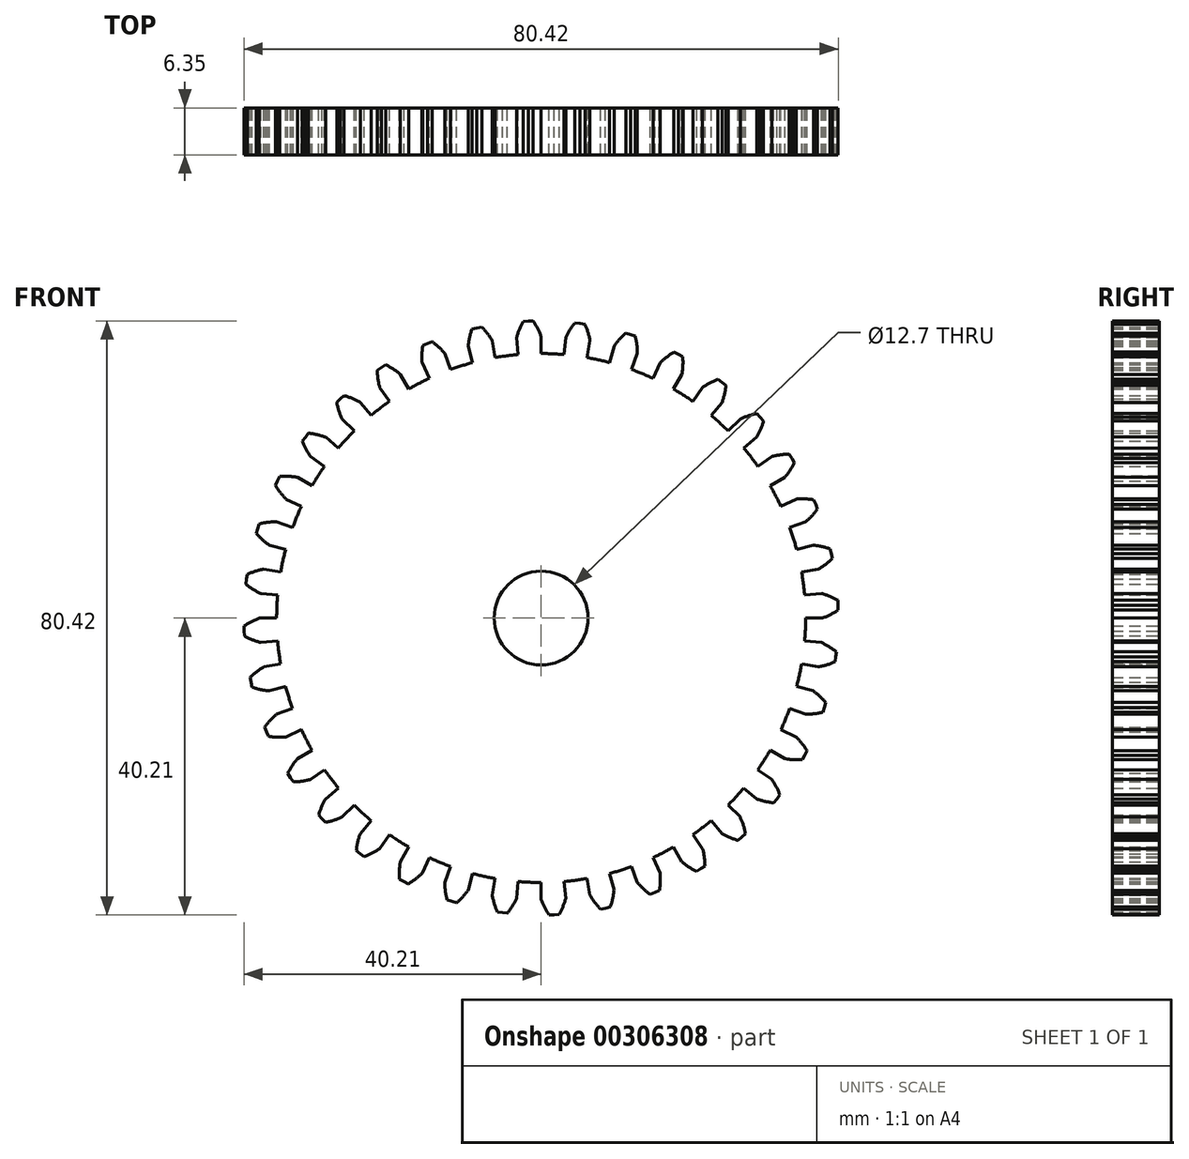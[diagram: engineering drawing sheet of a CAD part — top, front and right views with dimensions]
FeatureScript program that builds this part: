
annotation { "Feature Type Name" : "Feature", "Feature Type Description" : "" }
export const myFeature = defineFeature(function(context is Context, id is Id, definition is map)
    precondition{}
    {
        {
            var Q0;
            Q0=qCreatedBy(makeId("Front.planeOp"),FACE);
            var sketch = newSketch(context, id + "F0", { "sketchPlane" : qUnion([Q0])});
            skCircle(sketch, "E0", {"center": v(0, 0) * mm, "radius": 35.8 * mm});
            skArc(sketch, "E1.trimOffspring", {"start": v(0, 38.1) * mm, "mid": v(-0.47, 39.19) * mm, "end": v(-1.08, 40.2) * mm});
            skLineSegment(sketch, "E2", {"start": v(-1.08, 40.2) * mm, "end": v(-1.75, 40.19) * mm});
            skLineSegment(sketch, "E3", {"start": v(0, 38.1) * mm, "end": v(0, 35.8) * mm});
            skLineSegment(sketch, "E4.MirrorCS", {"start": v(-2.43, 40.15) * mm, "end": v(-1.75, 40.19) * mm});
            skArc(sketch, "E5.MirrorCS", {"start": v(-3.32, 37.96) * mm, "mid": v(-2.94, 39.08) * mm, "end": v(-2.43, 40.15) * mm});
            skLineSegment(sketch, "E6.MirrorCS", {"start": v(-3.32, 37.96) * mm, "end": v(-3.12, 35.67) * mm});
            skSolve(sketch);
        }
        {
            var Q0;
            {var subQ0=sQuery(id+"F0.wireOp",EDGE,"E0");var subQ1=makeQuery(id+"F0.imprint","INTERSECT",VERTEX,{"derivedFrom":[subQ0,sQuery(id+"F0.wireOp",EDGE,"E3")]});Q0=makeQuery(id+"F0.imprint","IMPRINT",FACE,{"disambiguationData":[TD([[makeQuery(id+"F0.imprint","IMPRINT",EDGE,{"disambiguationData":[TD([[subQ1,-1.0]])],"derivedFrom":subQ0}),1.0]])]});}
            cPlane(context, id + "F1", {"entities" : qUnion([Q0]), "cplaneType" : CPlaneType.OFFSET, "offset" : 6.35 * mm, "width" : 152.4 * mm, "height" : 152.4 * mm});
        }
        {
            var Q0;
            Q0=qCreatedBy(id+"F1.planeOp",FACE);
            var sketch = newSketch(context, id + "F2", { "sketchPlane" : qUnion([Q0])});
            skCircle(sketch, "E7.0", {"center": v(0, 0) * mm, "radius": 35.8 * mm});
            skArc(sketch, "E8.0.0", {"start": v(-3.12, 35.67) * mm, "mid": v(-1.56, 35.77) * mm, "end": v(0, 35.8) * mm});
            skLineSegment(sketch, "E8.0.1", {"start": v(0, 35.8) * mm, "end": v(0, 38.1) * mm});
            skArc(sketch, "E8.0.2", {"start": v(0, 38.1) * mm, "mid": v(-0.47, 39.19) * mm, "end": v(-1.08, 40.2) * mm});
            skLineSegment(sketch, "E8.0.3", {"start": v(-1.08, 40.2) * mm, "end": v(-1.75, 40.19) * mm});
            skLineSegment(sketch, "E8.0.4", {"start": v(-1.75, 40.19) * mm, "end": v(-2.43, 40.15) * mm});
            skArc(sketch, "E8.0.5", {"start": v(-2.43, 40.15) * mm, "mid": v(-2.94, 39.08) * mm, "end": v(-3.32, 37.96) * mm});
            skLineSegment(sketch, "E8.0.6", {"start": v(-3.32, 37.96) * mm, "end": v(-3.12, 35.67) * mm});
            skSolve(sketch);
        }
        {
            var Q0;
            {var subQ0=sQuery(id+"F2.wireOp",EDGE,"E8.0.1");Q0=makeQuery(id+"F2.imprint","IMPRINT",FACE,{"disambiguationData":[TD([[makeQuery(id+"F2.imprint","IMPRINT",EDGE,{"derivedFrom":subQ0}),1.0]])]});}
            var Q1;
            Q1=makeQuery(id+"F0.imprint","IMPRINT",FACE,{"disambiguationData":[TD([[makeQuery(id+"F0.imprint","IMPRINT",EDGE,{"derivedFrom":sQuery(id+"F0.wireOp",EDGE,"E1.trimOffspring")}),1.0]])]});
            loft(context, id + "F3", {"sheetProfilesArray" : [{ "sheetProfileEntities" : qUnion([Q0]) }, { "sheetProfileEntities" : qUnion([Q1]) }]});
        }
        {
            var Q0;
            Q0=qCreatedBy(id+"F1.planeOp",FACE);
            var sketch = newSketch(context, id + "F4", { "sketchPlane" : qUnion([Q0])});
            skCircle(sketch, "E9", {"center": v(0, 0) * mm, "radius": 35.8 * mm});
            skSolve(sketch);
        }
        {
            var Q0;
            Q0=makeQuery(id+"F4.imprint","IMPRINT",FACE,{"disambiguationData":[TD([[makeQuery(id+"F4.imprint","IMPRINT",EDGE,{"derivedFrom":sQuery(id+"F4.wireOp",EDGE,"E9")}),1.0]])]});
            var Q1;
            Q1=makeQuery(id+"F3.opLoft","CAP_FACE",FACE,{"disambiguationData":[OSD([makeQuery(id+"F0.imprint","IMPRINT",FACE,{"disambiguationData":[TD([[makeQuery(id+"F0.imprint","IMPRINT",EDGE,{"derivedFrom":sQuery(id+"F0.wireOp",EDGE,"E1.trimOffspring")}),1.0]])]})])],"isStart":true});
            extrude(context, id + "F5", {"entities" : qUnion([Q0]), "operationType" : NewBodyOperationType.ADD, "endBound" : BoundingType.UP_TO_SURFACE, "oppositeDirection" : true, "endBoundEntityFace" : qUnion([Q1]), "depth" : 25.4 * mm});
        }
        {
            var Q0;
            {var subQ0=sQuery(id+"F2.wireOp",EDGE,"E8.0.1");Q0=makeQuery(id+"F3.opLoft","SWEPT_BODY",BODY,{"disambiguationData":[OSD([makeQuery(id+"F0.imprint","IMPRINT",FACE,{"disambiguationData":[TD([[makeQuery(id+"F0.imprint","IMPRINT",EDGE,{"derivedFrom":sQuery(id+"F0.wireOp",EDGE,"E1.trimOffspring")}),1.0]])]}),makeQuery(id+"F2.imprint","IMPRINT",FACE,{"disambiguationData":[TD([[makeQuery(id+"F2.imprint","IMPRINT",EDGE,{"derivedFrom":subQ0}),1.0]])]})])]});}
            var Q1;
            Q1=makeQuery(id+"F5.opExtrude","SWEPT_FACE",FACE,{"disambiguationData":[OSD([sQuery(id+"F4.wireOp",EDGE,"E9")])]});
            circularPattern(context, id + "F6", {"entities" : qUnion([Q0]), "axis" : qUnion([Q1]), "angle" : 360 * degree, "instanceCount" : 36, "equalSpace" : true});
        }
        {
            var Q0;
            {var subQ0=sQuery(id+"F2.wireOp",EDGE,"E8.0.1");Q0=makeQuery(id+"F6.opPattern","COPY",BODY,{"derivedFrom":makeQuery(id+"F3.opLoft","SWEPT_BODY",BODY,{"disambiguationData":[OSD([makeQuery(id+"F0.imprint","IMPRINT",FACE,{"disambiguationData":[TD([[makeQuery(id+"F0.imprint","IMPRINT",EDGE,{"derivedFrom":sQuery(id+"F0.wireOp",EDGE,"E1.trimOffspring")}),1.0]])]}),makeQuery(id+"F2.imprint","IMPRINT",FACE,{"disambiguationData":[TD([[makeQuery(id+"F2.imprint","IMPRINT",EDGE,{"derivedFrom":subQ0}),1.0]])]})])]}),"instanceName":"22"});}
            var Q1;
            {var subQ0=sQuery(id+"F2.wireOp",EDGE,"E8.0.1");Q1=makeQuery(id+"F3.opLoft","SWEPT_BODY",BODY,{"disambiguationData":[OSD([makeQuery(id+"F0.imprint","IMPRINT",FACE,{"disambiguationData":[TD([[makeQuery(id+"F0.imprint","IMPRINT",EDGE,{"derivedFrom":sQuery(id+"F0.wireOp",EDGE,"E1.trimOffspring")}),1.0]])]}),makeQuery(id+"F2.imprint","IMPRINT",FACE,{"disambiguationData":[TD([[makeQuery(id+"F2.imprint","IMPRINT",EDGE,{"derivedFrom":subQ0}),1.0]])]})])]});}
            var Q2;
            {var subQ0=sQuery(id+"F2.wireOp",EDGE,"E8.0.1");Q2=makeQuery(id+"F6.opPattern","COPY",BODY,{"derivedFrom":makeQuery(id+"F3.opLoft","SWEPT_BODY",BODY,{"disambiguationData":[OSD([makeQuery(id+"F0.imprint","IMPRINT",FACE,{"disambiguationData":[TD([[makeQuery(id+"F0.imprint","IMPRINT",EDGE,{"derivedFrom":sQuery(id+"F0.wireOp",EDGE,"E1.trimOffspring")}),1.0]])]}),makeQuery(id+"F2.imprint","IMPRINT",FACE,{"disambiguationData":[TD([[makeQuery(id+"F2.imprint","IMPRINT",EDGE,{"derivedFrom":subQ0}),1.0]])]})])]}),"instanceName":"35"});}
            var Q3;
            {var subQ0=sQuery(id+"F2.wireOp",EDGE,"E8.0.1");Q3=makeQuery(id+"F6.opPattern","COPY",BODY,{"derivedFrom":makeQuery(id+"F3.opLoft","SWEPT_BODY",BODY,{"disambiguationData":[OSD([makeQuery(id+"F0.imprint","IMPRINT",FACE,{"disambiguationData":[TD([[makeQuery(id+"F0.imprint","IMPRINT",EDGE,{"derivedFrom":sQuery(id+"F0.wireOp",EDGE,"E1.trimOffspring")}),1.0]])]}),makeQuery(id+"F2.imprint","IMPRINT",FACE,{"disambiguationData":[TD([[makeQuery(id+"F2.imprint","IMPRINT",EDGE,{"derivedFrom":subQ0}),1.0]])]})])]}),"instanceName":"34"});}
            var Q4;
            {var subQ0=sQuery(id+"F2.wireOp",EDGE,"E8.0.1");Q4=makeQuery(id+"F6.opPattern","COPY",BODY,{"derivedFrom":makeQuery(id+"F3.opLoft","SWEPT_BODY",BODY,{"disambiguationData":[OSD([makeQuery(id+"F0.imprint","IMPRINT",FACE,{"disambiguationData":[TD([[makeQuery(id+"F0.imprint","IMPRINT",EDGE,{"derivedFrom":sQuery(id+"F0.wireOp",EDGE,"E1.trimOffspring")}),1.0]])]}),makeQuery(id+"F2.imprint","IMPRINT",FACE,{"disambiguationData":[TD([[makeQuery(id+"F2.imprint","IMPRINT",EDGE,{"derivedFrom":subQ0}),1.0]])]})])]}),"instanceName":"33"});}
            var Q5;
            {var subQ0=sQuery(id+"F2.wireOp",EDGE,"E8.0.1");Q5=makeQuery(id+"F6.opPattern","COPY",BODY,{"derivedFrom":makeQuery(id+"F3.opLoft","SWEPT_BODY",BODY,{"disambiguationData":[OSD([makeQuery(id+"F0.imprint","IMPRINT",FACE,{"disambiguationData":[TD([[makeQuery(id+"F0.imprint","IMPRINT",EDGE,{"derivedFrom":sQuery(id+"F0.wireOp",EDGE,"E1.trimOffspring")}),1.0]])]}),makeQuery(id+"F2.imprint","IMPRINT",FACE,{"disambiguationData":[TD([[makeQuery(id+"F2.imprint","IMPRINT",EDGE,{"derivedFrom":subQ0}),1.0]])]})])]}),"instanceName":"32"});}
            var Q6;
            {var subQ0=sQuery(id+"F2.wireOp",EDGE,"E8.0.1");Q6=makeQuery(id+"F6.opPattern","COPY",BODY,{"derivedFrom":makeQuery(id+"F3.opLoft","SWEPT_BODY",BODY,{"disambiguationData":[OSD([makeQuery(id+"F0.imprint","IMPRINT",FACE,{"disambiguationData":[TD([[makeQuery(id+"F0.imprint","IMPRINT",EDGE,{"derivedFrom":sQuery(id+"F0.wireOp",EDGE,"E1.trimOffspring")}),1.0]])]}),makeQuery(id+"F2.imprint","IMPRINT",FACE,{"disambiguationData":[TD([[makeQuery(id+"F2.imprint","IMPRINT",EDGE,{"derivedFrom":subQ0}),1.0]])]})])]}),"instanceName":"31"});}
            var Q7;
            {var subQ0=sQuery(id+"F2.wireOp",EDGE,"E8.0.1");Q7=makeQuery(id+"F6.opPattern","COPY",BODY,{"derivedFrom":makeQuery(id+"F3.opLoft","SWEPT_BODY",BODY,{"disambiguationData":[OSD([makeQuery(id+"F0.imprint","IMPRINT",FACE,{"disambiguationData":[TD([[makeQuery(id+"F0.imprint","IMPRINT",EDGE,{"derivedFrom":sQuery(id+"F0.wireOp",EDGE,"E1.trimOffspring")}),1.0]])]}),makeQuery(id+"F2.imprint","IMPRINT",FACE,{"disambiguationData":[TD([[makeQuery(id+"F2.imprint","IMPRINT",EDGE,{"derivedFrom":subQ0}),1.0]])]})])]}),"instanceName":"30"});}
            var Q8;
            {var subQ0=sQuery(id+"F2.wireOp",EDGE,"E8.0.1");Q8=makeQuery(id+"F6.opPattern","COPY",BODY,{"derivedFrom":makeQuery(id+"F3.opLoft","SWEPT_BODY",BODY,{"disambiguationData":[OSD([makeQuery(id+"F0.imprint","IMPRINT",FACE,{"disambiguationData":[TD([[makeQuery(id+"F0.imprint","IMPRINT",EDGE,{"derivedFrom":sQuery(id+"F0.wireOp",EDGE,"E1.trimOffspring")}),1.0]])]}),makeQuery(id+"F2.imprint","IMPRINT",FACE,{"disambiguationData":[TD([[makeQuery(id+"F2.imprint","IMPRINT",EDGE,{"derivedFrom":subQ0}),1.0]])]})])]}),"instanceName":"29"});}
            var Q9;
            {var subQ0=sQuery(id+"F2.wireOp",EDGE,"E8.0.1");Q9=makeQuery(id+"F6.opPattern","COPY",BODY,{"derivedFrom":makeQuery(id+"F3.opLoft","SWEPT_BODY",BODY,{"disambiguationData":[OSD([makeQuery(id+"F0.imprint","IMPRINT",FACE,{"disambiguationData":[TD([[makeQuery(id+"F0.imprint","IMPRINT",EDGE,{"derivedFrom":sQuery(id+"F0.wireOp",EDGE,"E1.trimOffspring")}),1.0]])]}),makeQuery(id+"F2.imprint","IMPRINT",FACE,{"disambiguationData":[TD([[makeQuery(id+"F2.imprint","IMPRINT",EDGE,{"derivedFrom":subQ0}),1.0]])]})])]}),"instanceName":"28"});}
            var Q10;
            {var subQ0=sQuery(id+"F2.wireOp",EDGE,"E8.0.1");Q10=makeQuery(id+"F6.opPattern","COPY",BODY,{"derivedFrom":makeQuery(id+"F3.opLoft","SWEPT_BODY",BODY,{"disambiguationData":[OSD([makeQuery(id+"F0.imprint","IMPRINT",FACE,{"disambiguationData":[TD([[makeQuery(id+"F0.imprint","IMPRINT",EDGE,{"derivedFrom":sQuery(id+"F0.wireOp",EDGE,"E1.trimOffspring")}),1.0]])]}),makeQuery(id+"F2.imprint","IMPRINT",FACE,{"disambiguationData":[TD([[makeQuery(id+"F2.imprint","IMPRINT",EDGE,{"derivedFrom":subQ0}),1.0]])]})])]}),"instanceName":"27"});}
            var Q11;
            {var subQ0=sQuery(id+"F2.wireOp",EDGE,"E8.0.1");Q11=makeQuery(id+"F6.opPattern","COPY",BODY,{"derivedFrom":makeQuery(id+"F3.opLoft","SWEPT_BODY",BODY,{"disambiguationData":[OSD([makeQuery(id+"F0.imprint","IMPRINT",FACE,{"disambiguationData":[TD([[makeQuery(id+"F0.imprint","IMPRINT",EDGE,{"derivedFrom":sQuery(id+"F0.wireOp",EDGE,"E1.trimOffspring")}),1.0]])]}),makeQuery(id+"F2.imprint","IMPRINT",FACE,{"disambiguationData":[TD([[makeQuery(id+"F2.imprint","IMPRINT",EDGE,{"derivedFrom":subQ0}),1.0]])]})])]}),"instanceName":"1"});}
            var Q12;
            {var subQ0=sQuery(id+"F2.wireOp",EDGE,"E8.0.1");Q12=makeQuery(id+"F6.opPattern","COPY",BODY,{"derivedFrom":makeQuery(id+"F3.opLoft","SWEPT_BODY",BODY,{"disambiguationData":[OSD([makeQuery(id+"F0.imprint","IMPRINT",FACE,{"disambiguationData":[TD([[makeQuery(id+"F0.imprint","IMPRINT",EDGE,{"derivedFrom":sQuery(id+"F0.wireOp",EDGE,"E1.trimOffspring")}),1.0]])]}),makeQuery(id+"F2.imprint","IMPRINT",FACE,{"disambiguationData":[TD([[makeQuery(id+"F2.imprint","IMPRINT",EDGE,{"derivedFrom":subQ0}),1.0]])]})])]}),"instanceName":"2"});}
            var Q13;
            {var subQ0=sQuery(id+"F2.wireOp",EDGE,"E8.0.1");Q13=makeQuery(id+"F6.opPattern","COPY",BODY,{"derivedFrom":makeQuery(id+"F3.opLoft","SWEPT_BODY",BODY,{"disambiguationData":[OSD([makeQuery(id+"F0.imprint","IMPRINT",FACE,{"disambiguationData":[TD([[makeQuery(id+"F0.imprint","IMPRINT",EDGE,{"derivedFrom":sQuery(id+"F0.wireOp",EDGE,"E1.trimOffspring")}),1.0]])]}),makeQuery(id+"F2.imprint","IMPRINT",FACE,{"disambiguationData":[TD([[makeQuery(id+"F2.imprint","IMPRINT",EDGE,{"derivedFrom":subQ0}),1.0]])]})])]}),"instanceName":"3"});}
            var Q14;
            {var subQ0=sQuery(id+"F2.wireOp",EDGE,"E8.0.1");Q14=makeQuery(id+"F6.opPattern","COPY",BODY,{"derivedFrom":makeQuery(id+"F3.opLoft","SWEPT_BODY",BODY,{"disambiguationData":[OSD([makeQuery(id+"F0.imprint","IMPRINT",FACE,{"disambiguationData":[TD([[makeQuery(id+"F0.imprint","IMPRINT",EDGE,{"derivedFrom":sQuery(id+"F0.wireOp",EDGE,"E1.trimOffspring")}),1.0]])]}),makeQuery(id+"F2.imprint","IMPRINT",FACE,{"disambiguationData":[TD([[makeQuery(id+"F2.imprint","IMPRINT",EDGE,{"derivedFrom":subQ0}),1.0]])]})])]}),"instanceName":"4"});}
            var Q15;
            {var subQ0=sQuery(id+"F2.wireOp",EDGE,"E8.0.1");Q15=makeQuery(id+"F6.opPattern","COPY",BODY,{"derivedFrom":makeQuery(id+"F3.opLoft","SWEPT_BODY",BODY,{"disambiguationData":[OSD([makeQuery(id+"F0.imprint","IMPRINT",FACE,{"disambiguationData":[TD([[makeQuery(id+"F0.imprint","IMPRINT",EDGE,{"derivedFrom":sQuery(id+"F0.wireOp",EDGE,"E1.trimOffspring")}),1.0]])]}),makeQuery(id+"F2.imprint","IMPRINT",FACE,{"disambiguationData":[TD([[makeQuery(id+"F2.imprint","IMPRINT",EDGE,{"derivedFrom":subQ0}),1.0]])]})])]}),"instanceName":"5"});}
            var Q16;
            {var subQ0=sQuery(id+"F2.wireOp",EDGE,"E8.0.1");Q16=makeQuery(id+"F6.opPattern","COPY",BODY,{"derivedFrom":makeQuery(id+"F3.opLoft","SWEPT_BODY",BODY,{"disambiguationData":[OSD([makeQuery(id+"F0.imprint","IMPRINT",FACE,{"disambiguationData":[TD([[makeQuery(id+"F0.imprint","IMPRINT",EDGE,{"derivedFrom":sQuery(id+"F0.wireOp",EDGE,"E1.trimOffspring")}),1.0]])]}),makeQuery(id+"F2.imprint","IMPRINT",FACE,{"disambiguationData":[TD([[makeQuery(id+"F2.imprint","IMPRINT",EDGE,{"derivedFrom":subQ0}),1.0]])]})])]}),"instanceName":"6"});}
            var Q17;
            {var subQ0=sQuery(id+"F2.wireOp",EDGE,"E8.0.1");Q17=makeQuery(id+"F6.opPattern","COPY",BODY,{"derivedFrom":makeQuery(id+"F3.opLoft","SWEPT_BODY",BODY,{"disambiguationData":[OSD([makeQuery(id+"F0.imprint","IMPRINT",FACE,{"disambiguationData":[TD([[makeQuery(id+"F0.imprint","IMPRINT",EDGE,{"derivedFrom":sQuery(id+"F0.wireOp",EDGE,"E1.trimOffspring")}),1.0]])]}),makeQuery(id+"F2.imprint","IMPRINT",FACE,{"disambiguationData":[TD([[makeQuery(id+"F2.imprint","IMPRINT",EDGE,{"derivedFrom":subQ0}),1.0]])]})])]}),"instanceName":"7"});}
            var Q18;
            {var subQ0=sQuery(id+"F2.wireOp",EDGE,"E8.0.1");Q18=makeQuery(id+"F6.opPattern","COPY",BODY,{"derivedFrom":makeQuery(id+"F3.opLoft","SWEPT_BODY",BODY,{"disambiguationData":[OSD([makeQuery(id+"F0.imprint","IMPRINT",FACE,{"disambiguationData":[TD([[makeQuery(id+"F0.imprint","IMPRINT",EDGE,{"derivedFrom":sQuery(id+"F0.wireOp",EDGE,"E1.trimOffspring")}),1.0]])]}),makeQuery(id+"F2.imprint","IMPRINT",FACE,{"disambiguationData":[TD([[makeQuery(id+"F2.imprint","IMPRINT",EDGE,{"derivedFrom":subQ0}),1.0]])]})])]}),"instanceName":"8"});}
            var Q19;
            {var subQ0=sQuery(id+"F2.wireOp",EDGE,"E8.0.1");Q19=makeQuery(id+"F6.opPattern","COPY",BODY,{"derivedFrom":makeQuery(id+"F3.opLoft","SWEPT_BODY",BODY,{"disambiguationData":[OSD([makeQuery(id+"F0.imprint","IMPRINT",FACE,{"disambiguationData":[TD([[makeQuery(id+"F0.imprint","IMPRINT",EDGE,{"derivedFrom":sQuery(id+"F0.wireOp",EDGE,"E1.trimOffspring")}),1.0]])]}),makeQuery(id+"F2.imprint","IMPRINT",FACE,{"disambiguationData":[TD([[makeQuery(id+"F2.imprint","IMPRINT",EDGE,{"derivedFrom":subQ0}),1.0]])]})])]}),"instanceName":"9"});}
            var Q20;
            {var subQ0=sQuery(id+"F2.wireOp",EDGE,"E8.0.1");Q20=makeQuery(id+"F6.opPattern","COPY",BODY,{"derivedFrom":makeQuery(id+"F3.opLoft","SWEPT_BODY",BODY,{"disambiguationData":[OSD([makeQuery(id+"F0.imprint","IMPRINT",FACE,{"disambiguationData":[TD([[makeQuery(id+"F0.imprint","IMPRINT",EDGE,{"derivedFrom":sQuery(id+"F0.wireOp",EDGE,"E1.trimOffspring")}),1.0]])]}),makeQuery(id+"F2.imprint","IMPRINT",FACE,{"disambiguationData":[TD([[makeQuery(id+"F2.imprint","IMPRINT",EDGE,{"derivedFrom":subQ0}),1.0]])]})])]}),"instanceName":"10"});}
            var Q21;
            {var subQ0=sQuery(id+"F2.wireOp",EDGE,"E8.0.1");Q21=makeQuery(id+"F6.opPattern","COPY",BODY,{"derivedFrom":makeQuery(id+"F3.opLoft","SWEPT_BODY",BODY,{"disambiguationData":[OSD([makeQuery(id+"F0.imprint","IMPRINT",FACE,{"disambiguationData":[TD([[makeQuery(id+"F0.imprint","IMPRINT",EDGE,{"derivedFrom":sQuery(id+"F0.wireOp",EDGE,"E1.trimOffspring")}),1.0]])]}),makeQuery(id+"F2.imprint","IMPRINT",FACE,{"disambiguationData":[TD([[makeQuery(id+"F2.imprint","IMPRINT",EDGE,{"derivedFrom":subQ0}),1.0]])]})])]}),"instanceName":"26"});}
            var Q22;
            {var subQ0=sQuery(id+"F2.wireOp",EDGE,"E8.0.1");Q22=makeQuery(id+"F6.opPattern","COPY",BODY,{"derivedFrom":makeQuery(id+"F3.opLoft","SWEPT_BODY",BODY,{"disambiguationData":[OSD([makeQuery(id+"F0.imprint","IMPRINT",FACE,{"disambiguationData":[TD([[makeQuery(id+"F0.imprint","IMPRINT",EDGE,{"derivedFrom":sQuery(id+"F0.wireOp",EDGE,"E1.trimOffspring")}),1.0]])]}),makeQuery(id+"F2.imprint","IMPRINT",FACE,{"disambiguationData":[TD([[makeQuery(id+"F2.imprint","IMPRINT",EDGE,{"derivedFrom":subQ0}),1.0]])]})])]}),"instanceName":"25"});}
            var Q23;
            {var subQ0=sQuery(id+"F2.wireOp",EDGE,"E8.0.1");Q23=makeQuery(id+"F6.opPattern","COPY",BODY,{"derivedFrom":makeQuery(id+"F3.opLoft","SWEPT_BODY",BODY,{"disambiguationData":[OSD([makeQuery(id+"F0.imprint","IMPRINT",FACE,{"disambiguationData":[TD([[makeQuery(id+"F0.imprint","IMPRINT",EDGE,{"derivedFrom":sQuery(id+"F0.wireOp",EDGE,"E1.trimOffspring")}),1.0]])]}),makeQuery(id+"F2.imprint","IMPRINT",FACE,{"disambiguationData":[TD([[makeQuery(id+"F2.imprint","IMPRINT",EDGE,{"derivedFrom":subQ0}),1.0]])]})])]}),"instanceName":"24"});}
            var Q24;
            {var subQ0=sQuery(id+"F2.wireOp",EDGE,"E8.0.1");Q24=makeQuery(id+"F6.opPattern","COPY",BODY,{"derivedFrom":makeQuery(id+"F3.opLoft","SWEPT_BODY",BODY,{"disambiguationData":[OSD([makeQuery(id+"F0.imprint","IMPRINT",FACE,{"disambiguationData":[TD([[makeQuery(id+"F0.imprint","IMPRINT",EDGE,{"derivedFrom":sQuery(id+"F0.wireOp",EDGE,"E1.trimOffspring")}),1.0]])]}),makeQuery(id+"F2.imprint","IMPRINT",FACE,{"disambiguationData":[TD([[makeQuery(id+"F2.imprint","IMPRINT",EDGE,{"derivedFrom":subQ0}),1.0]])]})])]}),"instanceName":"23"});}
            var Q25;
            {var subQ0=sQuery(id+"F2.wireOp",EDGE,"E8.0.1");Q25=makeQuery(id+"F6.opPattern","COPY",BODY,{"derivedFrom":makeQuery(id+"F3.opLoft","SWEPT_BODY",BODY,{"disambiguationData":[OSD([makeQuery(id+"F0.imprint","IMPRINT",FACE,{"disambiguationData":[TD([[makeQuery(id+"F0.imprint","IMPRINT",EDGE,{"derivedFrom":sQuery(id+"F0.wireOp",EDGE,"E1.trimOffspring")}),1.0]])]}),makeQuery(id+"F2.imprint","IMPRINT",FACE,{"disambiguationData":[TD([[makeQuery(id+"F2.imprint","IMPRINT",EDGE,{"derivedFrom":subQ0}),1.0]])]})])]}),"instanceName":"21"});}
            var Q26;
            {var subQ0=sQuery(id+"F2.wireOp",EDGE,"E8.0.1");Q26=makeQuery(id+"F6.opPattern","COPY",BODY,{"derivedFrom":makeQuery(id+"F3.opLoft","SWEPT_BODY",BODY,{"disambiguationData":[OSD([makeQuery(id+"F0.imprint","IMPRINT",FACE,{"disambiguationData":[TD([[makeQuery(id+"F0.imprint","IMPRINT",EDGE,{"derivedFrom":sQuery(id+"F0.wireOp",EDGE,"E1.trimOffspring")}),1.0]])]}),makeQuery(id+"F2.imprint","IMPRINT",FACE,{"disambiguationData":[TD([[makeQuery(id+"F2.imprint","IMPRINT",EDGE,{"derivedFrom":subQ0}),1.0]])]})])]}),"instanceName":"19"});}
            var Q27;
            {var subQ0=sQuery(id+"F2.wireOp",EDGE,"E8.0.1");Q27=makeQuery(id+"F6.opPattern","COPY",BODY,{"derivedFrom":makeQuery(id+"F3.opLoft","SWEPT_BODY",BODY,{"disambiguationData":[OSD([makeQuery(id+"F0.imprint","IMPRINT",FACE,{"disambiguationData":[TD([[makeQuery(id+"F0.imprint","IMPRINT",EDGE,{"derivedFrom":sQuery(id+"F0.wireOp",EDGE,"E1.trimOffspring")}),1.0]])]}),makeQuery(id+"F2.imprint","IMPRINT",FACE,{"disambiguationData":[TD([[makeQuery(id+"F2.imprint","IMPRINT",EDGE,{"derivedFrom":subQ0}),1.0]])]})])]}),"instanceName":"18"});}
            var Q28;
            {var subQ0=sQuery(id+"F2.wireOp",EDGE,"E8.0.1");Q28=makeQuery(id+"F6.opPattern","COPY",BODY,{"derivedFrom":makeQuery(id+"F3.opLoft","SWEPT_BODY",BODY,{"disambiguationData":[OSD([makeQuery(id+"F0.imprint","IMPRINT",FACE,{"disambiguationData":[TD([[makeQuery(id+"F0.imprint","IMPRINT",EDGE,{"derivedFrom":sQuery(id+"F0.wireOp",EDGE,"E1.trimOffspring")}),1.0]])]}),makeQuery(id+"F2.imprint","IMPRINT",FACE,{"disambiguationData":[TD([[makeQuery(id+"F2.imprint","IMPRINT",EDGE,{"derivedFrom":subQ0}),1.0]])]})])]}),"instanceName":"17"});}
            var Q29;
            {var subQ0=sQuery(id+"F2.wireOp",EDGE,"E8.0.1");Q29=makeQuery(id+"F6.opPattern","COPY",BODY,{"derivedFrom":makeQuery(id+"F3.opLoft","SWEPT_BODY",BODY,{"disambiguationData":[OSD([makeQuery(id+"F0.imprint","IMPRINT",FACE,{"disambiguationData":[TD([[makeQuery(id+"F0.imprint","IMPRINT",EDGE,{"derivedFrom":sQuery(id+"F0.wireOp",EDGE,"E1.trimOffspring")}),1.0]])]}),makeQuery(id+"F2.imprint","IMPRINT",FACE,{"disambiguationData":[TD([[makeQuery(id+"F2.imprint","IMPRINT",EDGE,{"derivedFrom":subQ0}),1.0]])]})])]}),"instanceName":"16"});}
            var Q30;
            {var subQ0=sQuery(id+"F2.wireOp",EDGE,"E8.0.1");Q30=makeQuery(id+"F6.opPattern","COPY",BODY,{"derivedFrom":makeQuery(id+"F3.opLoft","SWEPT_BODY",BODY,{"disambiguationData":[OSD([makeQuery(id+"F0.imprint","IMPRINT",FACE,{"disambiguationData":[TD([[makeQuery(id+"F0.imprint","IMPRINT",EDGE,{"derivedFrom":sQuery(id+"F0.wireOp",EDGE,"E1.trimOffspring")}),1.0]])]}),makeQuery(id+"F2.imprint","IMPRINT",FACE,{"disambiguationData":[TD([[makeQuery(id+"F2.imprint","IMPRINT",EDGE,{"derivedFrom":subQ0}),1.0]])]})])]}),"instanceName":"15"});}
            var Q31;
            {var subQ0=sQuery(id+"F2.wireOp",EDGE,"E8.0.1");Q31=makeQuery(id+"F6.opPattern","COPY",BODY,{"derivedFrom":makeQuery(id+"F3.opLoft","SWEPT_BODY",BODY,{"disambiguationData":[OSD([makeQuery(id+"F0.imprint","IMPRINT",FACE,{"disambiguationData":[TD([[makeQuery(id+"F0.imprint","IMPRINT",EDGE,{"derivedFrom":sQuery(id+"F0.wireOp",EDGE,"E1.trimOffspring")}),1.0]])]}),makeQuery(id+"F2.imprint","IMPRINT",FACE,{"disambiguationData":[TD([[makeQuery(id+"F2.imprint","IMPRINT",EDGE,{"derivedFrom":subQ0}),1.0]])]})])]}),"instanceName":"14"});}
            var Q32;
            {var subQ0=sQuery(id+"F2.wireOp",EDGE,"E8.0.1");Q32=makeQuery(id+"F6.opPattern","COPY",BODY,{"derivedFrom":makeQuery(id+"F3.opLoft","SWEPT_BODY",BODY,{"disambiguationData":[OSD([makeQuery(id+"F0.imprint","IMPRINT",FACE,{"disambiguationData":[TD([[makeQuery(id+"F0.imprint","IMPRINT",EDGE,{"derivedFrom":sQuery(id+"F0.wireOp",EDGE,"E1.trimOffspring")}),1.0]])]}),makeQuery(id+"F2.imprint","IMPRINT",FACE,{"disambiguationData":[TD([[makeQuery(id+"F2.imprint","IMPRINT",EDGE,{"derivedFrom":subQ0}),1.0]])]})])]}),"instanceName":"11"});}
            var Q33;
            {var subQ0=sQuery(id+"F2.wireOp",EDGE,"E8.0.1");Q33=makeQuery(id+"F6.opPattern","COPY",BODY,{"derivedFrom":makeQuery(id+"F3.opLoft","SWEPT_BODY",BODY,{"disambiguationData":[OSD([makeQuery(id+"F0.imprint","IMPRINT",FACE,{"disambiguationData":[TD([[makeQuery(id+"F0.imprint","IMPRINT",EDGE,{"derivedFrom":sQuery(id+"F0.wireOp",EDGE,"E1.trimOffspring")}),1.0]])]}),makeQuery(id+"F2.imprint","IMPRINT",FACE,{"disambiguationData":[TD([[makeQuery(id+"F2.imprint","IMPRINT",EDGE,{"derivedFrom":subQ0}),1.0]])]})])]}),"instanceName":"12"});}
            var Q34;
            {var subQ0=sQuery(id+"F2.wireOp",EDGE,"E8.0.1");Q34=makeQuery(id+"F6.opPattern","COPY",BODY,{"derivedFrom":makeQuery(id+"F3.opLoft","SWEPT_BODY",BODY,{"disambiguationData":[OSD([makeQuery(id+"F0.imprint","IMPRINT",FACE,{"disambiguationData":[TD([[makeQuery(id+"F0.imprint","IMPRINT",EDGE,{"derivedFrom":sQuery(id+"F0.wireOp",EDGE,"E1.trimOffspring")}),1.0]])]}),makeQuery(id+"F2.imprint","IMPRINT",FACE,{"disambiguationData":[TD([[makeQuery(id+"F2.imprint","IMPRINT",EDGE,{"derivedFrom":subQ0}),1.0]])]})])]}),"instanceName":"13"});}
            var Q35;
            {var subQ0=sQuery(id+"F2.wireOp",EDGE,"E8.0.1");Q35=makeQuery(id+"F6.opPattern","COPY",BODY,{"derivedFrom":makeQuery(id+"F3.opLoft","SWEPT_BODY",BODY,{"disambiguationData":[OSD([makeQuery(id+"F0.imprint","IMPRINT",FACE,{"disambiguationData":[TD([[makeQuery(id+"F0.imprint","IMPRINT",EDGE,{"derivedFrom":sQuery(id+"F0.wireOp",EDGE,"E1.trimOffspring")}),1.0]])]}),makeQuery(id+"F2.imprint","IMPRINT",FACE,{"disambiguationData":[TD([[makeQuery(id+"F2.imprint","IMPRINT",EDGE,{"derivedFrom":subQ0}),1.0]])]})])]}),"instanceName":"20"});}
            booleanBodies(context, id + "F7", {"operationType" : BooleanOperationType.UNION, "tools" : qUnion([Q0, Q1, Q2, Q3, Q4, Q5, Q6, Q7, Q8, Q9, Q10, Q11, Q12, Q13, Q14, Q15, Q16, Q17, Q18, Q19, Q20, Q21, Q22, Q23, Q24, Q25, Q26, Q27, Q28, Q29, Q30, Q31, Q32, Q33, Q34, Q35])});
        }
        {
            var Q0;
            {var subQ0=sQuery(id+"F2.wireOp",EDGE,"E8.0.1");var subQ3=makeQuery(id+"F5.boolean.opBoolean","MERGE",FACE,{"derivedFrom":[makeQuery(id+"F3.opLoft","CAP_FACE",FACE,{"disambiguationData":[OSD([makeQuery(id+"F2.imprint","IMPRINT",FACE,{"disambiguationData":[TD([[makeQuery(id+"F2.imprint","IMPRINT",EDGE,{"derivedFrom":subQ0}),1.0]])]})])],"isStart":true}),makeQuery(id+"F5.opExtrude","CAP_FACE",FACE,{"disambiguationData":[OSD([sQuery(id+"F4.wireOp",EDGE,"E9")])],"isStart":true})]});Q0=makeQuery(id+"F7.opBoolean","MERGE",FACE,{"derivedFrom":[subQ3,makeQuery(id+"F6.opPattern","COPY",FACE,{"derivedFrom":subQ3,"instanceName":"1"}),makeQuery(id+"F6.opPattern","COPY",FACE,{"derivedFrom":subQ3,"instanceName":"2"}),makeQuery(id+"F6.opPattern","COPY",FACE,{"derivedFrom":subQ3,"instanceName":"3"}),makeQuery(id+"F6.opPattern","COPY",FACE,{"derivedFrom":subQ3,"instanceName":"4"}),makeQuery(id+"F6.opPattern","COPY",FACE,{"derivedFrom":subQ3,"instanceName":"5"}),makeQuery(id+"F6.opPattern","COPY",FACE,{"derivedFrom":subQ3,"instanceName":"6"}),makeQuery(id+"F6.opPattern","COPY",FACE,{"derivedFrom":subQ3,"instanceName":"7"}),makeQuery(id+"F6.opPattern","COPY",FACE,{"derivedFrom":subQ3,"instanceName":"8"}),makeQuery(id+"F6.opPattern","COPY",FACE,{"derivedFrom":subQ3,"instanceName":"9"}),makeQuery(id+"F6.opPattern","COPY",FACE,{"derivedFrom":subQ3,"instanceName":"10"}),makeQuery(id+"F6.opPattern","COPY",FACE,{"derivedFrom":subQ3,"instanceName":"11"}),makeQuery(id+"F6.opPattern","COPY",FACE,{"derivedFrom":subQ3,"instanceName":"12"}),makeQuery(id+"F6.opPattern","COPY",FACE,{"derivedFrom":subQ3,"instanceName":"13"}),makeQuery(id+"F6.opPattern","COPY",FACE,{"derivedFrom":subQ3,"instanceName":"14"}),makeQuery(id+"F6.opPattern","COPY",FACE,{"derivedFrom":subQ3,"instanceName":"15"}),makeQuery(id+"F6.opPattern","COPY",FACE,{"derivedFrom":subQ3,"instanceName":"16"}),makeQuery(id+"F6.opPattern","COPY",FACE,{"derivedFrom":subQ3,"instanceName":"17"}),makeQuery(id+"F6.opPattern","COPY",FACE,{"derivedFrom":subQ3,"instanceName":"18"}),makeQuery(id+"F6.opPattern","COPY",FACE,{"derivedFrom":subQ3,"instanceName":"19"}),makeQuery(id+"F6.opPattern","COPY",FACE,{"derivedFrom":subQ3,"instanceName":"20"}),makeQuery(id+"F6.opPattern","COPY",FACE,{"derivedFrom":subQ3,"instanceName":"21"}),makeQuery(id+"F6.opPattern","COPY",FACE,{"derivedFrom":subQ3,"instanceName":"22"}),makeQuery(id+"F6.opPattern","COPY",FACE,{"derivedFrom":subQ3,"instanceName":"23"}),makeQuery(id+"F6.opPattern","COPY",FACE,{"derivedFrom":subQ3,"instanceName":"24"}),makeQuery(id+"F6.opPattern","COPY",FACE,{"derivedFrom":subQ3,"instanceName":"25"}),makeQuery(id+"F6.opPattern","COPY",FACE,{"derivedFrom":subQ3,"instanceName":"26"}),makeQuery(id+"F6.opPattern","COPY",FACE,{"derivedFrom":subQ3,"instanceName":"27"}),makeQuery(id+"F6.opPattern","COPY",FACE,{"derivedFrom":subQ3,"instanceName":"28"}),makeQuery(id+"F6.opPattern","COPY",FACE,{"derivedFrom":subQ3,"instanceName":"29"}),makeQuery(id+"F6.opPattern","COPY",FACE,{"derivedFrom":subQ3,"instanceName":"30"}),makeQuery(id+"F6.opPattern","COPY",FACE,{"derivedFrom":subQ3,"instanceName":"31"}),makeQuery(id+"F6.opPattern","COPY",FACE,{"derivedFrom":subQ3,"instanceName":"32"}),makeQuery(id+"F6.opPattern","COPY",FACE,{"derivedFrom":subQ3,"instanceName":"33"}),makeQuery(id+"F6.opPattern","COPY",FACE,{"derivedFrom":subQ3,"instanceName":"34"}),makeQuery(id+"F6.opPattern","COPY",FACE,{"derivedFrom":subQ3,"instanceName":"35"})]});}
            var sketch = newSketch(context, id + "F8", { "sketchPlane" : qUnion([Q0])});
            skPoint(sketch, "E10", {"position": v(0, 0) * mm});
            skSolve(sketch);
        }
        {
            var Q0;
            Q0=sQuery(id+"F8.wireOp",VERTEX,"E10");
            var Q1;
            {var subQ0=sQuery(id+"F2.wireOp",EDGE,"E8.0.1");Q1=makeQuery(id+"F6.opPattern","COPY",BODY,{"derivedFrom":makeQuery(id+"F3.opLoft","SWEPT_BODY",BODY,{"disambiguationData":[OSD([makeQuery(id+"F0.imprint","IMPRINT",FACE,{"disambiguationData":[TD([[makeQuery(id+"F0.imprint","IMPRINT",EDGE,{"derivedFrom":sQuery(id+"F0.wireOp",EDGE,"E1.trimOffspring")}),1.0]])]}),makeQuery(id+"F2.imprint","IMPRINT",FACE,{"disambiguationData":[TD([[makeQuery(id+"F2.imprint","IMPRINT",EDGE,{"derivedFrom":subQ0}),1.0]])]})])]}),"instanceName":"22"});}
            hole(context, id + "F9", {"style" : HoleStyle.SIMPLE, "endStyle" : HoleEndStyle.THROUGH, "holeDiameter" : 12.7 * mm, "tappedDepth" : 12.7 * mm, "tapClearance" : 3, "locations" : qUnion([Q0]), "scope" : qUnion([Q1])});
        }
    });
